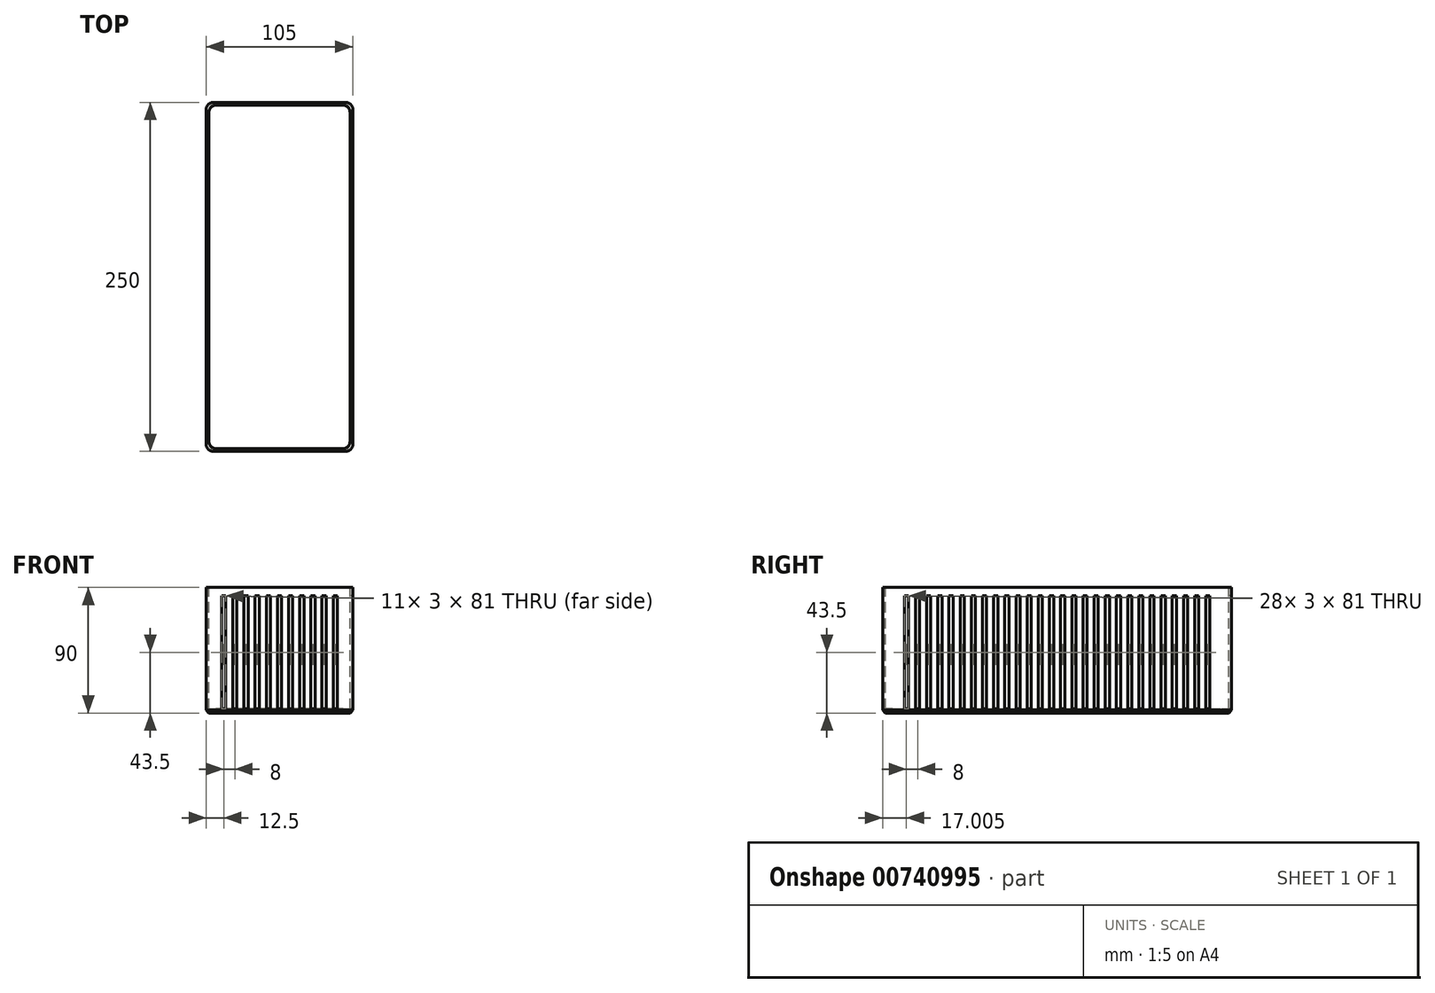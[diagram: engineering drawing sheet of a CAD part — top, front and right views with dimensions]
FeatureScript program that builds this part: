
annotation { "Feature Type Name" : "Feature", "Feature Type Description" : "" }
export const myFeature = defineFeature(function(context is Context, id is Id, definition is map)
    precondition{}
    {
        {
            var Q0;
            Q0=qCreatedBy(makeId("Top.planeOp"),FACE);
            var sketch = newSketch(context, id + "F0", { "sketchPlane" : qUnion([Q0])});
            skLineSegment(sketch, "E0.bottom", {"start": v(-56.87, 197.97) * mm, "end": v(48.13, 197.97) * mm});
            skLineSegment(sketch, "E0.top", {"start": v(-56.87, -52.03) * mm, "end": v(48.13, -52.03) * mm});
            skLineSegment(sketch, "E0.left", {"start": v(-56.87, 197.97) * mm, "end": v(-56.87, -52.03) * mm});
            skLineSegment(sketch, "E0.right", {"start": v(48.13, 197.97) * mm, "end": v(48.13, -52.03) * mm});
            skSolve(sketch);
        }
        {
            var Q0;
            Q0=qSketchRegion(id+"F0",true);
            extrude(context, id + "F1", {"entities" : qUnion([Q0]), "depth" : 90 * mm, "offsetDistance" : 25 * mm});
        }
        {
            var Q0;
            Q0=makeQuery(id+"F1.opExtrude","CAP_FACE",FACE,{"disambiguationData":[OSD([sQuery(id+"F0.wireOp",EDGE,"E0.bottom"),sQuery(id+"F0.wireOp",EDGE,"E0.top"),sQuery(id+"F0.wireOp",EDGE,"E0.left"),sQuery(id+"F0.wireOp",EDGE,"E0.right")])],"isStart":false});
            var sketch = newSketch(context, id + "F2", { "sketchPlane" : qUnion([Q0])});
            skLineSegment(sketch, "E1.bottom", {"start": v(46.13, -50.03) * mm, "end": v(-54.87, -50.03) * mm});
            skLineSegment(sketch, "E1.top", {"start": v(46.13, 195.97) * mm, "end": v(-54.87, 195.97) * mm});
            skLineSegment(sketch, "E1.left", {"start": v(46.13, -50.03) * mm, "end": v(46.13, 195.97) * mm});
            skLineSegment(sketch, "E1.right", {"start": v(-54.87, -50.03) * mm, "end": v(-54.87, 195.97) * mm});
            skSolve(sketch);
        }
        {
            var Q0;
            Q0=qSketchRegion(id+"F2",true);
            extrude(context, id + "F3", {"entities" : qUnion([Q0]), "operationType" : NewBodyOperationType.REMOVE, "oppositeDirection" : true, "depth" : 87 * mm, "offsetDistance" : 25 * mm});
        }
        {
            var Q0;
            Q0=makeQuery(id+"F1.opExtrude","SWEPT_EDGE",EDGE,{"disambiguationData":[OSD([sQuery(id+"F0.wireOp",EDGE,"E0.top"),sQuery(id+"F0.wireOp",EDGE,"E0.right")])]});
            var Q1;
            Q1=makeQuery(id+"F1.opExtrude","SWEPT_EDGE",EDGE,{"disambiguationData":[OSD([sQuery(id+"F0.wireOp",EDGE,"E0.top"),sQuery(id+"F0.wireOp",EDGE,"E0.left")])]});
            var Q2;
            Q2=makeQuery(id+"F1.opExtrude","SWEPT_EDGE",EDGE,{"disambiguationData":[OSD([sQuery(id+"F0.wireOp",EDGE,"E0.bottom"),sQuery(id+"F0.wireOp",EDGE,"E0.right")])]});
            var Q3;
            Q3=makeQuery(id+"F1.opExtrude","SWEPT_EDGE",EDGE,{"disambiguationData":[OSD([sQuery(id+"F0.wireOp",EDGE,"E0.bottom"),sQuery(id+"F0.wireOp",EDGE,"E0.left")])]});
            fillet(context, id + "F4", {"entities" : qUnion([Q0, Q1, Q2, Q3]), "radius" : 5 * mm, "tangentPropagation" : true, "allowEdgeOverflow" : false});
        }
        {
            var Q0;
            Q0=makeQuery(id+"F3.boolean.opBoolean","COPY",EDGE,{"derivedFrom":makeQuery(id+"F3.opExtrude","SWEPT_EDGE",EDGE,{"disambiguationData":[OSD([sQuery(id+"F2.wireOp",EDGE,"E1.top"),sQuery(id+"F2.wireOp",EDGE,"E1.right")])]})});
            var Q1;
            Q1=makeQuery(id+"F3.boolean.opBoolean","COPY",EDGE,{"derivedFrom":makeQuery(id+"F3.opExtrude","SWEPT_EDGE",EDGE,{"disambiguationData":[OSD([sQuery(id+"F2.wireOp",EDGE,"E1.top"),sQuery(id+"F2.wireOp",EDGE,"E1.left")])]})});
            var Q2;
            Q2=makeQuery(id+"F3.boolean.opBoolean","COPY",EDGE,{"derivedFrom":makeQuery(id+"F3.opExtrude","SWEPT_EDGE",EDGE,{"disambiguationData":[OSD([sQuery(id+"F2.wireOp",EDGE,"E1.bottom"),sQuery(id+"F2.wireOp",EDGE,"E1.right")])]})});
            var Q3;
            Q3=makeQuery(id+"F3.boolean.opBoolean","COPY",EDGE,{"derivedFrom":makeQuery(id+"F3.opExtrude","SWEPT_EDGE",EDGE,{"disambiguationData":[OSD([sQuery(id+"F2.wireOp",EDGE,"E1.bottom"),sQuery(id+"F2.wireOp",EDGE,"E1.left")])]})});
            fillet(context, id + "F5", {"entities" : qUnion([Q0, Q1, Q2, Q3]), "radius" : 5 * mm, "tangentPropagation" : true, "allowEdgeOverflow" : false});
        }
        {
            var Q0;
            Q0=makeQuery(id+"F1.opExtrude","CAP_FACE",FACE,{"disambiguationData":[OSD([sQuery(id+"F0.wireOp",EDGE,"E0.bottom"),sQuery(id+"F0.wireOp",EDGE,"E0.top"),sQuery(id+"F0.wireOp",EDGE,"E0.left"),sQuery(id+"F0.wireOp",EDGE,"E0.right")])],"isStart":true});
            chamfer(context, id + "F6", {"entities" : qUnion([Q0]), "width" : 2 * mm, "tangentPropagation" : true});
        }
        {
            var Q0;
            Q0=makeQuery(id+"F1.opExtrude","SWEPT_FACE",FACE,{"disambiguationData":[OSD([sQuery(id+"F0.wireOp",EDGE,"E0.top")])]});
            var sketch = newSketch(context, id + "F7", { "sketchPlane" : qUnion([Q0])});
            skLineSegment(sketch, "E2.bottom", {"start": v(-45.87, 84) * mm, "end": v(-42.87, 84) * mm});
            skLineSegment(sketch, "E2.top", {"start": v(-45.87, 3) * mm, "end": v(-42.87, 3) * mm});
            skLineSegment(sketch, "E2.left", {"start": v(-45.87, 84) * mm, "end": v(-45.87, 3) * mm});
            skLineSegment(sketch, "E2.right", {"start": v(-42.87, 84) * mm, "end": v(-42.87, 3) * mm});
            skLineSegment(sketch, "E3.bottom", {"start": v(-37.87, 84) * mm, "end": v(-34.87, 84) * mm});
            skLineSegment(sketch, "E3.top", {"start": v(-37.87, 3) * mm, "end": v(-34.87, 3) * mm});
            skLineSegment(sketch, "E3.left", {"start": v(-37.87, 84) * mm, "end": v(-37.87, 3) * mm});
            skLineSegment(sketch, "E3.right", {"start": v(-34.87, 84) * mm, "end": v(-34.87, 3) * mm});
            skLineSegment(sketch, "E4.bottom", {"start": v(-29.87, 84) * mm, "end": v(-26.87, 84) * mm});
            skLineSegment(sketch, "E4.top", {"start": v(-29.87, 3) * mm, "end": v(-26.87, 3) * mm});
            skLineSegment(sketch, "E4.left", {"start": v(-29.87, 84) * mm, "end": v(-29.87, 3) * mm});
            skLineSegment(sketch, "E4.right", {"start": v(-26.87, 84) * mm, "end": v(-26.87, 3) * mm});
            skLineSegment(sketch, "E5.bottom", {"start": v(-21.87, 84) * mm, "end": v(-18.87, 84) * mm});
            skLineSegment(sketch, "E5.top", {"start": v(-21.87, 3) * mm, "end": v(-18.87, 3) * mm});
            skLineSegment(sketch, "E5.left", {"start": v(-21.87, 84) * mm, "end": v(-21.87, 3) * mm});
            skLineSegment(sketch, "E5.right", {"start": v(-18.87, 84) * mm, "end": v(-18.87, 3) * mm});
            skLineSegment(sketch, "E6.bottom", {"start": v(-13.87, 84) * mm, "end": v(-10.87, 84) * mm});
            skLineSegment(sketch, "E6.top", {"start": v(-13.87, 3) * mm, "end": v(-10.87, 3) * mm});
            skLineSegment(sketch, "E6.left", {"start": v(-13.87, 84) * mm, "end": v(-13.87, 3) * mm});
            skLineSegment(sketch, "E6.right", {"start": v(-10.87, 84) * mm, "end": v(-10.87, 3) * mm});
            skLineSegment(sketch, "E7", {"start": v(-49.25, 3) * mm, "end": v(38.95, 3) * mm, "construction": true});
            skLineSegment(sketch, "E8", {"start": v(-49.84, 84) * mm, "end": v(37.94, 84) * mm, "construction": true});
            skPoint(sketch, "E8.endSnap0", {"position": v(-28.37, 84) * mm});
            skLineSegment(sketch, "E9.bottom", {"start": v(-5.87, 84) * mm, "end": v(-2.87, 84) * mm});
            skLineSegment(sketch, "E9.top", {"start": v(-5.87, 3) * mm, "end": v(-2.87, 3) * mm});
            skLineSegment(sketch, "E9.left", {"start": v(-5.87, 84) * mm, "end": v(-5.87, 3) * mm});
            skLineSegment(sketch, "E9.right", {"start": v(-2.87, 84) * mm, "end": v(-2.87, 3) * mm});
            skLineSegment(sketch, "E10.bottom", {"start": v(2.13, 84) * mm, "end": v(5.13, 84) * mm});
            skLineSegment(sketch, "E10.top", {"start": v(2.13, 3) * mm, "end": v(5.13, 3) * mm});
            skLineSegment(sketch, "E10.left", {"start": v(2.13, 84) * mm, "end": v(2.13, 3) * mm});
            skLineSegment(sketch, "E10.right", {"start": v(5.13, 84) * mm, "end": v(5.13, 3) * mm});
            skLineSegment(sketch, "E11.bottom", {"start": v(10.13, 84) * mm, "end": v(13.13, 84) * mm});
            skLineSegment(sketch, "E11.top", {"start": v(10.13, 3) * mm, "end": v(13.13, 3) * mm});
            skLineSegment(sketch, "E11.left", {"start": v(10.13, 84) * mm, "end": v(10.13, 3) * mm});
            skLineSegment(sketch, "E11.right", {"start": v(13.13, 84) * mm, "end": v(13.13, 3) * mm});
            skLineSegment(sketch, "E12.bottom", {"start": v(18.13, 84) * mm, "end": v(21.13, 84) * mm});
            skLineSegment(sketch, "E12.top", {"start": v(18.13, 3) * mm, "end": v(21.13, 3) * mm});
            skLineSegment(sketch, "E12.left", {"start": v(18.13, 84) * mm, "end": v(18.13, 3) * mm});
            skLineSegment(sketch, "E12.right", {"start": v(21.13, 84) * mm, "end": v(21.13, 3) * mm});
            skLineSegment(sketch, "E13.bottom", {"start": v(26.13, 84) * mm, "end": v(29.13, 84) * mm});
            skLineSegment(sketch, "E13.top", {"start": v(26.13, 3) * mm, "end": v(29.13, 3) * mm});
            skLineSegment(sketch, "E13.left", {"start": v(26.13, 84) * mm, "end": v(26.13, 3) * mm});
            skLineSegment(sketch, "E13.right", {"start": v(29.13, 84) * mm, "end": v(29.13, 3) * mm});
            skPoint(sketch, "E14.endSnap0", {"position": v(11.63, 84) * mm});
            skLineSegment(sketch, "E15.bottom", {"start": v(34.13, 84) * mm, "end": v(37.13, 84) * mm});
            skLineSegment(sketch, "E15.top", {"start": v(34.13, 3) * mm, "end": v(37.13, 3) * mm});
            skLineSegment(sketch, "E15.left", {"start": v(34.13, 84) * mm, "end": v(34.13, 3) * mm});
            skLineSegment(sketch, "E15.right", {"start": v(37.13, 84) * mm, "end": v(37.13, 3) * mm});
            skSolve(sketch);
        }
        {
            var Q0;
            Q0 = qSketchRegion(id + "F7", true);
            extrude(context, id + "F8", {"entities" : qUnion([Q0]), "operationType" : NewBodyOperationType.REMOVE, "oppositeDirection" : true, "depth" : 300 * mm, "offsetDistance" : 25 * mm});
        }
        {
            var Q0;
            Q0=makeQuery(id+"F1.opExtrude","SWEPT_FACE",FACE,{"disambiguationData":[OSD([sQuery(id+"F0.wireOp",EDGE,"E0.left")])]});
            var sketch = newSketch(context, id + "F9", { "sketchPlane" : qUnion([Q0])});
            skLineSegment(sketch, "E16.bottom", {"start": v(-182.47, 84) * mm, "end": v(-179.47, 84) * mm});
            skLineSegment(sketch, "E16.top", {"start": v(-182.47, 3) * mm, "end": v(-179.47, 3) * mm});
            skLineSegment(sketch, "E16.left", {"start": v(-182.47, 84) * mm, "end": v(-182.47, 3) * mm});
            skLineSegment(sketch, "E16.right", {"start": v(-179.47, 84) * mm, "end": v(-179.47, 3) * mm});
            skLineSegment(sketch, "E17", {"start": v(-192.97, 3) * mm, "end": v(47.03, 3) * mm, "construction": true});
            skLineSegment(sketch, "E18", {"start": v(-192.97, 84) * mm, "end": v(47.03, 84) * mm, "construction": true});
            skLineSegment(sketch, "E19.bottom", {"start": v(-174.47, 84) * mm, "end": v(-171.47, 84) * mm});
            skLineSegment(sketch, "E19.top", {"start": v(-174.47, 3) * mm, "end": v(-171.47, 3) * mm});
            skLineSegment(sketch, "E19.left", {"start": v(-174.47, 84) * mm, "end": v(-174.47, 3) * mm});
            skLineSegment(sketch, "E19.right", {"start": v(-171.47, 84) * mm, "end": v(-171.47, 3) * mm});
            skLineSegment(sketch, "E20.bottom", {"start": v(-166.47, 84) * mm, "end": v(-163.47, 84) * mm});
            skLineSegment(sketch, "E20.top", {"start": v(-166.47, 3) * mm, "end": v(-163.47, 3) * mm});
            skLineSegment(sketch, "E20.left", {"start": v(-166.47, 84) * mm, "end": v(-166.47, 3) * mm});
            skLineSegment(sketch, "E20.right", {"start": v(-163.47, 84) * mm, "end": v(-163.47, 3) * mm});
            skLineSegment(sketch, "E21.bottom", {"start": v(-158.47, 84) * mm, "end": v(-155.47, 84) * mm});
            skLineSegment(sketch, "E21.top", {"start": v(-158.47, 3) * mm, "end": v(-155.47, 3) * mm});
            skLineSegment(sketch, "E21.left", {"start": v(-158.47, 84) * mm, "end": v(-158.47, 3) * mm});
            skLineSegment(sketch, "E21.right", {"start": v(-155.47, 84) * mm, "end": v(-155.47, 3) * mm});
            skLineSegment(sketch, "E22.bottom", {"start": v(-150.47, 84) * mm, "end": v(-147.47, 84) * mm});
            skLineSegment(sketch, "E22.top", {"start": v(-150.47, 3) * mm, "end": v(-147.47, 3) * mm});
            skLineSegment(sketch, "E22.left", {"start": v(-150.47, 84) * mm, "end": v(-150.47, 3) * mm});
            skLineSegment(sketch, "E22.right", {"start": v(-147.47, 84) * mm, "end": v(-147.47, 3) * mm});
            skLineSegment(sketch, "E23.bottom", {"start": v(-142.47, 84) * mm, "end": v(-139.47, 84) * mm});
            skLineSegment(sketch, "E23.top", {"start": v(-142.47, 3) * mm, "end": v(-139.47, 3) * mm});
            skLineSegment(sketch, "E23.left", {"start": v(-142.47, 84) * mm, "end": v(-142.47, 3) * mm});
            skLineSegment(sketch, "E23.right", {"start": v(-139.47, 84) * mm, "end": v(-139.47, 3) * mm});
            skPoint(sketch, "E24.endSnap0", {"position": v(-156.97, 84) * mm});
            skLineSegment(sketch, "E25.bottom", {"start": v(-134.47, 84) * mm, "end": v(-131.47, 84) * mm});
            skLineSegment(sketch, "E25.top", {"start": v(-134.47, 3) * mm, "end": v(-131.47, 3) * mm});
            skLineSegment(sketch, "E25.left", {"start": v(-134.47, 84) * mm, "end": v(-134.47, 3) * mm});
            skLineSegment(sketch, "E25.right", {"start": v(-131.47, 84) * mm, "end": v(-131.47, 3) * mm});
            skLineSegment(sketch, "E26.bottom", {"start": v(-126.47, 84) * mm, "end": v(-123.47, 84) * mm});
            skLineSegment(sketch, "E26.top", {"start": v(-126.47, 3) * mm, "end": v(-123.47, 3) * mm});
            skLineSegment(sketch, "E26.left", {"start": v(-126.47, 84) * mm, "end": v(-126.47, 3) * mm});
            skLineSegment(sketch, "E26.right", {"start": v(-123.47, 84) * mm, "end": v(-123.47, 3) * mm});
            skLineSegment(sketch, "E27.bottom", {"start": v(-118.47, 84) * mm, "end": v(-115.47, 84) * mm});
            skLineSegment(sketch, "E27.top", {"start": v(-118.47, 3) * mm, "end": v(-115.47, 3) * mm});
            skLineSegment(sketch, "E27.left", {"start": v(-118.47, 84) * mm, "end": v(-118.47, 3) * mm});
            skLineSegment(sketch, "E27.right", {"start": v(-115.47, 84) * mm, "end": v(-115.47, 3) * mm});
            skLineSegment(sketch, "E28.bottom", {"start": v(-110.47, 84) * mm, "end": v(-107.47, 84) * mm});
            skLineSegment(sketch, "E28.top", {"start": v(-110.47, 3) * mm, "end": v(-107.47, 3) * mm});
            skLineSegment(sketch, "E28.left", {"start": v(-110.47, 84) * mm, "end": v(-110.47, 3) * mm});
            skLineSegment(sketch, "E28.right", {"start": v(-107.47, 84) * mm, "end": v(-107.47, 3) * mm});
            skLineSegment(sketch, "E29.bottom", {"start": v(-102.47, 84) * mm, "end": v(-99.47, 84) * mm});
            skLineSegment(sketch, "E29.top", {"start": v(-102.47, 3) * mm, "end": v(-99.47, 3) * mm});
            skLineSegment(sketch, "E29.left", {"start": v(-102.47, 84) * mm, "end": v(-102.47, 3) * mm});
            skLineSegment(sketch, "E29.right", {"start": v(-99.47, 84) * mm, "end": v(-99.47, 3) * mm});
            skPoint(sketch, "E30.endSnap0", {"position": v(-116.97, 84) * mm});
            skLineSegment(sketch, "E31.bottom", {"start": v(-94.47, 84) * mm, "end": v(-91.47, 84) * mm});
            skLineSegment(sketch, "E31.top", {"start": v(-94.47, 3) * mm, "end": v(-91.47, 3) * mm});
            skLineSegment(sketch, "E31.left", {"start": v(-94.47, 84) * mm, "end": v(-94.47, 3) * mm});
            skLineSegment(sketch, "E31.right", {"start": v(-91.47, 84) * mm, "end": v(-91.47, 3) * mm});
            skLineSegment(sketch, "E32.bottom", {"start": v(-86.47, 84) * mm, "end": v(-83.47, 84) * mm});
            skLineSegment(sketch, "E32.top", {"start": v(-86.47, 3) * mm, "end": v(-83.47, 3) * mm});
            skLineSegment(sketch, "E32.left", {"start": v(-86.47, 84) * mm, "end": v(-86.47, 3) * mm});
            skLineSegment(sketch, "E32.right", {"start": v(-83.47, 84) * mm, "end": v(-83.47, 3) * mm});
            skLineSegment(sketch, "E33.bottom", {"start": v(-78.47, 84) * mm, "end": v(-75.47, 84) * mm});
            skLineSegment(sketch, "E33.top", {"start": v(-78.47, 3) * mm, "end": v(-75.47, 3) * mm});
            skLineSegment(sketch, "E33.left", {"start": v(-78.47, 84) * mm, "end": v(-78.47, 3) * mm});
            skLineSegment(sketch, "E33.right", {"start": v(-75.47, 84) * mm, "end": v(-75.47, 3) * mm});
            skLineSegment(sketch, "E34.bottom", {"start": v(-70.47, 84) * mm, "end": v(-67.47, 84) * mm});
            skLineSegment(sketch, "E34.top", {"start": v(-70.47, 3) * mm, "end": v(-67.47, 3) * mm});
            skLineSegment(sketch, "E34.left", {"start": v(-70.47, 84) * mm, "end": v(-70.47, 3) * mm});
            skLineSegment(sketch, "E34.right", {"start": v(-67.47, 84) * mm, "end": v(-67.47, 3) * mm});
            skLineSegment(sketch, "E35.bottom", {"start": v(-62.47, 84) * mm, "end": v(-59.47, 84) * mm});
            skLineSegment(sketch, "E35.top", {"start": v(-62.47, 3) * mm, "end": v(-59.47, 3) * mm});
            skLineSegment(sketch, "E35.left", {"start": v(-62.47, 84) * mm, "end": v(-62.47, 3) * mm});
            skLineSegment(sketch, "E35.right", {"start": v(-59.47, 84) * mm, "end": v(-59.47, 3) * mm});
            skLineSegment(sketch, "E36.bottom", {"start": v(-54.47, 84) * mm, "end": v(-51.47, 84) * mm});
            skLineSegment(sketch, "E36.top", {"start": v(-54.47, 3) * mm, "end": v(-51.47, 3) * mm});
            skLineSegment(sketch, "E36.left", {"start": v(-54.47, 84) * mm, "end": v(-54.47, 3) * mm});
            skLineSegment(sketch, "E36.right", {"start": v(-51.47, 84) * mm, "end": v(-51.47, 3) * mm});
            skLineSegment(sketch, "E37.bottom", {"start": v(-46.47, 84) * mm, "end": v(-43.47, 84) * mm});
            skLineSegment(sketch, "E37.top", {"start": v(-46.47, 3) * mm, "end": v(-43.47, 3) * mm});
            skLineSegment(sketch, "E37.left", {"start": v(-46.47, 84) * mm, "end": v(-46.47, 3) * mm});
            skLineSegment(sketch, "E37.right", {"start": v(-43.47, 84) * mm, "end": v(-43.47, 3) * mm});
            skPoint(sketch, "E38.endSnap0", {"position": v(-60.97, 84) * mm});
            skLineSegment(sketch, "E39.bottom", {"start": v(-38.47, 84) * mm, "end": v(-35.47, 84) * mm});
            skLineSegment(sketch, "E39.top", {"start": v(-38.47, 3) * mm, "end": v(-35.47, 3) * mm});
            skLineSegment(sketch, "E39.left", {"start": v(-38.47, 84) * mm, "end": v(-38.47, 3) * mm});
            skLineSegment(sketch, "E39.right", {"start": v(-35.47, 84) * mm, "end": v(-35.47, 3) * mm});
            skLineSegment(sketch, "E40.bottom", {"start": v(-30.47, 84) * mm, "end": v(-27.47, 84) * mm});
            skLineSegment(sketch, "E40.top", {"start": v(-30.47, 3) * mm, "end": v(-27.47, 3) * mm});
            skLineSegment(sketch, "E40.left", {"start": v(-30.47, 84) * mm, "end": v(-30.47, 3) * mm});
            skLineSegment(sketch, "E40.right", {"start": v(-27.47, 84) * mm, "end": v(-27.47, 3) * mm});
            skLineSegment(sketch, "E41.bottom", {"start": v(-22.47, 84) * mm, "end": v(-19.47, 84) * mm});
            skLineSegment(sketch, "E41.top", {"start": v(-22.47, 3) * mm, "end": v(-19.47, 3) * mm});
            skLineSegment(sketch, "E41.left", {"start": v(-22.47, 84) * mm, "end": v(-22.47, 3) * mm});
            skLineSegment(sketch, "E41.right", {"start": v(-19.47, 84) * mm, "end": v(-19.47, 3) * mm});
            skLineSegment(sketch, "E42.bottom", {"start": v(-14.47, 84) * mm, "end": v(-11.47, 84) * mm});
            skLineSegment(sketch, "E42.top", {"start": v(-14.47, 3) * mm, "end": v(-11.47, 3) * mm});
            skLineSegment(sketch, "E42.left", {"start": v(-14.47, 84) * mm, "end": v(-14.47, 3) * mm});
            skLineSegment(sketch, "E42.right", {"start": v(-11.47, 84) * mm, "end": v(-11.47, 3) * mm});
            skLineSegment(sketch, "E43.bottom", {"start": v(-6.47, 84) * mm, "end": v(-3.47, 84) * mm});
            skLineSegment(sketch, "E43.top", {"start": v(-6.47, 3) * mm, "end": v(-3.47, 3) * mm});
            skLineSegment(sketch, "E43.left", {"start": v(-6.47, 84) * mm, "end": v(-6.47, 3) * mm});
            skLineSegment(sketch, "E43.right", {"start": v(-3.47, 84) * mm, "end": v(-3.47, 3) * mm});
            skPoint(sketch, "E44.endSnap0", {"position": v(-20.97, 84) * mm});
            skLineSegment(sketch, "E45.bottom", {"start": v(1.53, 84) * mm, "end": v(4.53, 84) * mm});
            skLineSegment(sketch, "E45.top", {"start": v(1.53, 3) * mm, "end": v(4.53, 3) * mm});
            skLineSegment(sketch, "E45.left", {"start": v(1.53, 84) * mm, "end": v(1.53, 3) * mm});
            skLineSegment(sketch, "E45.right", {"start": v(4.53, 84) * mm, "end": v(4.53, 3) * mm});
            skLineSegment(sketch, "E46.bottom", {"start": v(9.53, 84) * mm, "end": v(12.53, 84) * mm});
            skLineSegment(sketch, "E46.top", {"start": v(9.53, 3) * mm, "end": v(12.53, 3) * mm});
            skLineSegment(sketch, "E46.left", {"start": v(9.53, 84) * mm, "end": v(9.53, 3) * mm});
            skLineSegment(sketch, "E46.right", {"start": v(12.53, 84) * mm, "end": v(12.53, 3) * mm});
            skLineSegment(sketch, "E47.bottom", {"start": v(17.53, 84) * mm, "end": v(20.53, 84) * mm});
            skLineSegment(sketch, "E47.top", {"start": v(17.53, 3) * mm, "end": v(20.53, 3) * mm});
            skLineSegment(sketch, "E47.left", {"start": v(17.53, 84) * mm, "end": v(17.53, 3) * mm});
            skLineSegment(sketch, "E47.right", {"start": v(20.53, 84) * mm, "end": v(20.53, 3) * mm});
            skLineSegment(sketch, "E48.bottom", {"start": v(25.53, 84) * mm, "end": v(28.53, 84) * mm});
            skLineSegment(sketch, "E48.top", {"start": v(25.53, 3) * mm, "end": v(28.53, 3) * mm});
            skLineSegment(sketch, "E48.left", {"start": v(25.53, 84) * mm, "end": v(25.53, 3) * mm});
            skLineSegment(sketch, "E48.right", {"start": v(28.53, 84) * mm, "end": v(28.53, 3) * mm});
            skPoint(sketch, "E49.endSnap0", {"position": v(11.03, 84) * mm});
            skLineSegment(sketch, "E50.bottom", {"start": v(33.53, 84) * mm, "end": v(36.53, 84) * mm});
            skLineSegment(sketch, "E50.top", {"start": v(33.53, 3) * mm, "end": v(36.53, 3) * mm});
            skLineSegment(sketch, "E50.left", {"start": v(33.53, 84) * mm, "end": v(33.53, 3) * mm});
            skLineSegment(sketch, "E50.right", {"start": v(36.53, 84) * mm, "end": v(36.53, 3) * mm});
            skSolve(sketch);
        }
        {
            var Q0;
            Q0 = qSketchRegion(id + "F9", true);
            extrude(context, id + "F10", {"entities" : qUnion([Q0]), "operationType" : NewBodyOperationType.REMOVE, "oppositeDirection" : true, "depth" : 105 * mm, "offsetDistance" : 25 * mm});
        }
    });
